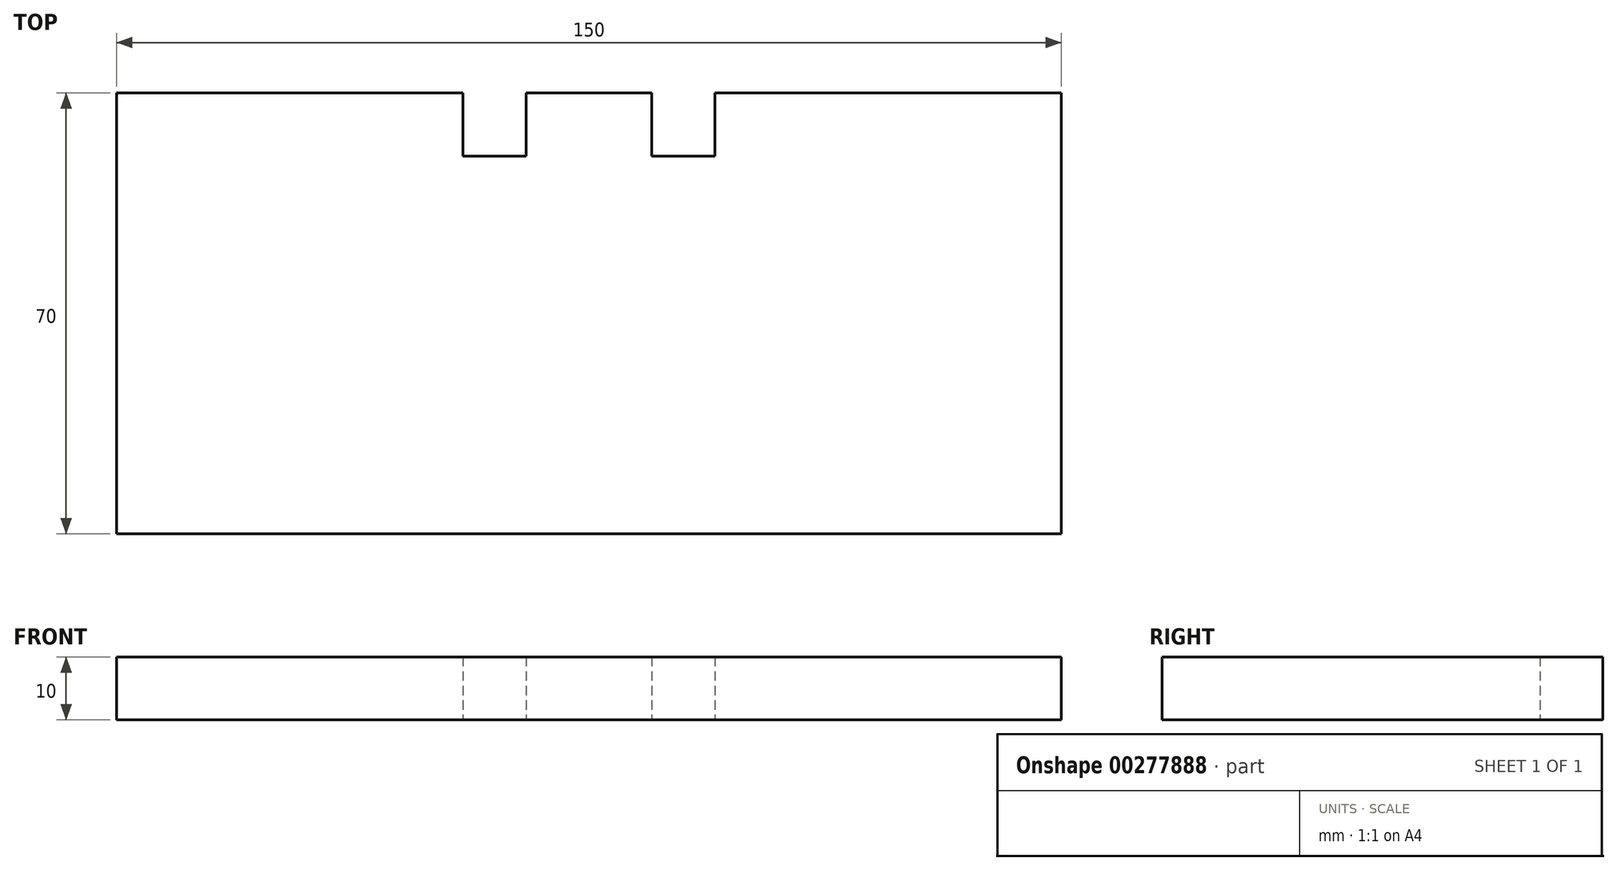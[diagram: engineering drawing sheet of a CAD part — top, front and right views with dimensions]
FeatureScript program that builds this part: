
annotation { "Feature Type Name" : "Feature", "Feature Type Description" : "" }
export const myFeature = defineFeature(function(context is Context, id is Id, definition is map)
    precondition{}
    {
        {
            var Q0;
            Q0=qCreatedBy(makeId("Top.planeOp"),FACE);
            var sketch = newSketch(context, id + "F0", { "sketchPlane" : qUnion([Q0])});
            skLineSegment(sketch, "E0", {"start": v(-55.56, -13.08) * mm, "end": v(-0.56, -13.08) * mm});
            skLineSegment(sketch, "E1", {"start": v(-0.56, -13.08) * mm, "end": v(-0.56, -23.08) * mm});
            skLineSegment(sketch, "E2", {"start": v(-0.56, -23.08) * mm, "end": v(9.44, -23.08) * mm});
            skLineSegment(sketch, "E3", {"start": v(9.44, -23.08) * mm, "end": v(9.44, -13.08) * mm});
            skLineSegment(sketch, "E4", {"start": v(9.44, -13.08) * mm, "end": v(29.44, -13.08) * mm});
            skLineSegment(sketch, "E5", {"start": v(29.44, -13.08) * mm, "end": v(29.44, -23.08) * mm});
            skLineSegment(sketch, "E6", {"start": v(29.44, -23.08) * mm, "end": v(39.44, -23.08) * mm});
            skLineSegment(sketch, "E7", {"start": v(39.44, -23.08) * mm, "end": v(39.44, -13.08) * mm});
            skLineSegment(sketch, "E8", {"start": v(39.44, -13.08) * mm, "end": v(94.44, -13.08) * mm});
            skLineSegment(sketch, "E9", {"start": v(94.44, -13.08) * mm, "end": v(94.44, -83.08) * mm});
            skLineSegment(sketch, "E10", {"start": v(94.44, -83.08) * mm, "end": v(-55.56, -83.08) * mm});
            skLineSegment(sketch, "E11", {"start": v(-55.56, -83.08) * mm, "end": v(-55.56, -13.08) * mm});
            skSolve(sketch);
        }
        {
            var Q0;
            Q0 = qSketchRegion(id + "F0", true);
            extrude(context, id + "F1", {"entities" : qUnion([Q0]), "depth" : 10 * mm});
        }
    });
